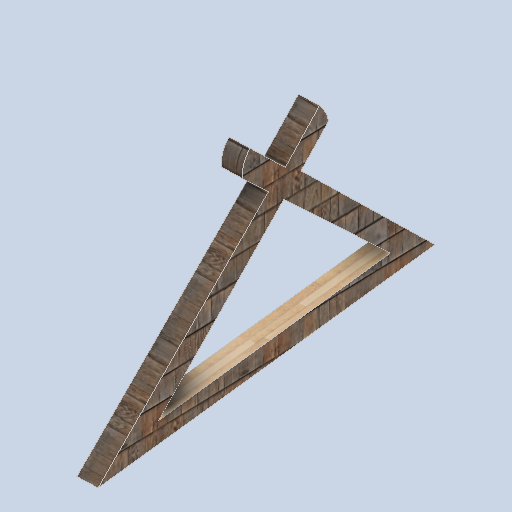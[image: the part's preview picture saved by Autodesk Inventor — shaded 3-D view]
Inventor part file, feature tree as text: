
AUTODESK INVENTOR PART (.ipt)
format: ipt  version: 2024.2 (Build 282272000, 272)  size: 528,384 bytes
history: native  units: mm
features: sketch x12, plane x8, extrude x5, projected_geometry x3, loft x2, other x1
ambient origin geometry x8: Origin, YZ Plane, XZ Plane, XY Plane, X Axis, Y Axis, Z Axis, Center Point
bodies: Solid1 (feature_tree)
feature tree (31):
  sketch  "Sketch1"  dims[d5=0.0mm d6=-7900.0mm d7=800.0mm]
  plane  "Work Plane2"
  loft  "Loft1"
  plane  "Work Plane3"
  extrude  "Extrusion1"  Depth=9000.0mm
  plane  "Work Plane4"
  sketch  "Sketch5"  dims[d12=800.0mm d13=0.0mm d14=90.0deg]
  plane  "Work Plane5"
  extrude  "Extrusion2"  Depth=9000.0mm
  plane  "Work Plane6"
  sketch  "Sketch7"  dims[d18=0.0mm d19=0.0mm d20=0.0mm]
  loft  "Loft2"
  extrude  "Extrusion3"  Depth=2500.0mm
  sketch  "Sketch10"  dims[d25=0.0mm d26=90.0deg]
  extrude  "Extrusion4"  TaperAngle=0.0deg  [1 undecoded]
  plane  "Work Plane7"
  extrude  "Extrusion5"  TaperAngle=0.0deg  [1 undecoded]
  plane  "Work Plane8"
  sketch  "Sketch14"  dims[d31=0.0mm d32=0.0mm d35=150.0mm d36=0.0mm d37=-75.0mm d38=500.0mm d39=0.872665mm d40=500.0mm d41=0.872665mm]
  plane  "Work Plane1"
  sketch  "Sketch2"  dims[d8=9000.0mm d9=9000.0mm]
  sketch  "Sketch3"  dims[d10=9000.0mm d11=9000.0mm]
  sketch  "Sketch6"  dims[d15=0.0mm d16=90.0deg d17=2500.0mm]
  projected_geometry  "Projected Loop1"
  sketch  "Sketch8"  dims[d21=6.981317mm d22=0.0mm d23=0.0mm]
  projected_geometry  "Projected Loop2"
  other  "Edges1"
  sketch  "Sketch9"  dims[d24=90.0deg]
  projected_geometry  "Projected Loop3"
  sketch  "Sketch11"  dims[d27=0.0mm d28=90.0deg]
  sketch  "Sketch12"  dims[d29=1.0mm d30=0.0mm]
note: 2 required parameter values undecoded (feature->parameter linkage not recoverable at this tier; creation-order binding heuristic only, values carry confidence <= 0.55)
